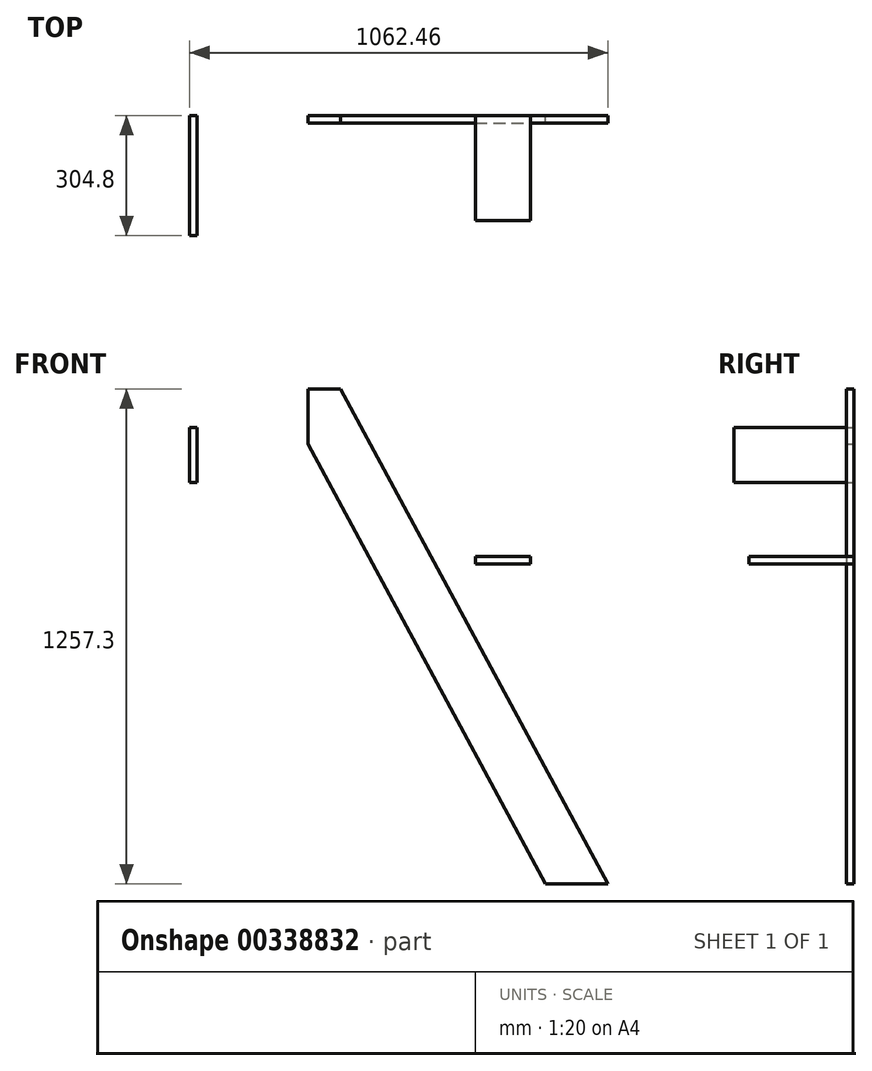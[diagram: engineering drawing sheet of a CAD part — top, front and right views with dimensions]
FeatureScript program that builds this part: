
annotation { "Feature Type Name" : "Feature", "Feature Type Description" : "" }
export const myFeature = defineFeature(function(context is Context, id is Id, definition is map)
    precondition{}
    {
        {
            var Q0;
            Q0=qCreatedBy(makeId("Front.planeOp"),FACE);
            var sketch = newSketch(context, id + "F0", { "sketchPlane" : qUnion([Q0])});
            skLineSegment(sketch, "E0", {"start": v(-245.7, 120.5) * mm, "end": v(-245.7, 260.2) * mm});
            skLineSegment(sketch, "E1", {"start": v(-245.7, 260.2) * mm, "end": v(-162.35, 260.2) * mm});
            skLineSegment(sketch, "E2", {"start": v(-162.35, 260.2) * mm, "end": v(516.3, -997.1) * mm});
            skLineSegment(sketch, "E3", {"start": v(516.3, -997.1) * mm, "end": v(357.55, -997.1) * mm});
            skLineSegment(sketch, "E4", {"start": v(357.55, -997.1) * mm, "end": v(-245.7, 120.5) * mm});
            skLineSegment(sketch, "E5.bottom", {"start": v(179.7, -164.66) * mm, "end": v(319.4, -164.66) * mm});
            skLineSegment(sketch, "E5.top", {"start": v(179.7, -183.71) * mm, "end": v(319.4, -183.71) * mm});
            skLineSegment(sketch, "E5.left", {"start": v(179.7, -164.66) * mm, "end": v(179.7, -183.71) * mm});
            skLineSegment(sketch, "E5.right", {"start": v(319.4, -164.66) * mm, "end": v(319.4, -183.71) * mm});
            skLineSegment(sketch, "E6.bottom", {"start": v(-546.16, 162.31) * mm, "end": v(-527.11, 162.31) * mm});
            skLineSegment(sketch, "E6.top", {"start": v(-546.16, 22.61) * mm, "end": v(-527.11, 22.61) * mm});
            skLineSegment(sketch, "E6.left", {"start": v(-546.16, 162.31) * mm, "end": v(-546.16, 22.61) * mm});
            skLineSegment(sketch, "E6.right", {"start": v(-527.11, 162.31) * mm, "end": v(-527.11, 22.61) * mm});
            skSolve(sketch);
        }
        {
            var Q0;
            Q0=makeQuery(id+"F0.imprint","IMPRINT",FACE,{"disambiguationData":[TD([[makeQuery(id+"F0.imprint","IMPRINT",EDGE,{"derivedFrom":sQuery(id+"F0.wireOp",EDGE,"E0")}),-1.0]])]});
            extrude(context, id + "F1", {"entities" : qUnion([Q0]), "depth" : 19.05 * mm});
        }
        {
            var Q0;
            Q0=makeQuery(id+"F0.imprint","IMPRINT",FACE,{"disambiguationData":[TD([[makeQuery(id+"F0.imprint","IMPRINT",EDGE,{"derivedFrom":sQuery(id+"F0.wireOp",EDGE,"E5.bottom")}),-1.0]])]});
            extrude(context, id + "F2", {"entities" : qUnion([Q0]), "depth" : 266.7 * mm});
        }
        {
            var Q0;
            Q0=makeQuery(id+"F0.imprint","IMPRINT",FACE,{"disambiguationData":[TD([[makeQuery(id+"F0.imprint","IMPRINT",EDGE,{"derivedFrom":sQuery(id+"F0.wireOp",EDGE,"E6.bottom")}),-1.0]])]});
            extrude(context, id + "F3", {"entities" : qUnion([Q0]), "depth" : 304.8 * mm});
        }
    });
